# Revit family: Camera-Canon-CR_N300
name_source: partatom
category: Communication Devices
units: mm (PartAtom-declared; Revit-internal decimal feet)

## family parameters
Cut with Voids When Loaded = No
Host = Face
Maintain Annotation Orientation = No
OmniClass Number = 23.85.10.14.11.14
OmniClass Title = Digital Cameras
Part Type = Normal
Room Calculation Point = No
Round Connector Dimension = Use Diameter
Shared = No

## types (2) — shared parameters
Amperage = 0.625 A
Apparent Load = 15 VA
Aspect Ratio = SDI: 1920 x 1080, 1280 x 720 | HDMI: 3840 x 2160, 1920 x 1080, 1280 x 720 | IP: 3840 x 2160, 1920 x 1080, 1280 x 720, 640 x 360 | USB: 1920 x 1080, 1280 x 720, 640 x 360
Assembly Code = D5030900
Constraints = 1
Depth = 6.46 "
Description = Canon’s CR-N300 PTZ camera produces outstanding image quality and is equipped with powerful features and functions to be utilized in many industries including House of Worship, Education, Broadcast, Corporate, Events and more.
Height = 7.01 "
Housing = Plastic construction
Instruction Sheet Link = https://www.usa.canon.com
Keynote = 11 52 00
Lens = f=3.67 – 73.4 mm, F/1.8 – 2.8, 8-bladed circular aperture
Lens Finish = Screen - Canon - Black
Manufacturer = Canon U.S.A., Inc.
Material = Plastic Housing
Model = CR-N300
Mount Finish = Metal - Canon
Number of Poles = 1
Operating Humidity = 10% – 90% (without condensation)
Operating Temperature = 32°F to 104°F (0°C to 40°C)
Power Factor = 1
Product Documentation Link = https://downloads.canon.com
Product Name = PTZ & Remote Camera
Product Page URL = https://www.usa.canon.com
Trim Finish = Plastic - Canon - Black
URL = https://www.usa.canon.com
Version = 2020 - v1.0a
Voltage = 24 V
Voltage Notes = PoE: PoE+ power supply via LAN connector (IEEE802.3at compliant) – PoE cannot be used | External power source: 24V DC (using included AC adaptor)
Wattage = 15 W
Wattage Notes = PoE+ Input: Approx. 16.2W* max. (body only) | DC Input: Approx. 15.0W max. (body only)
Weight = 4.86 lbf
Width = 6.06 "
zero-valued in all types: Default Elevation

## per-type parameters (varying)
| type | Finish |
| CR-N300 - Black | Plastic - Canon - Black |
| CR-N300 - White | Plastic - Canon - White |

## geometry (parser evidence)
native form markers: Sweep x15
no freeform markers — native parametric forms only
